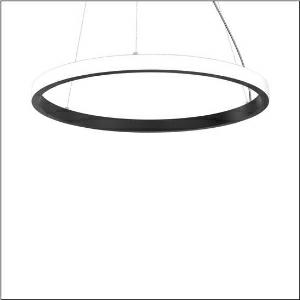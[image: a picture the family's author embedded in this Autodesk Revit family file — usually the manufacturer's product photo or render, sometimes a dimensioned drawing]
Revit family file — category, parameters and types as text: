
# Revit family: silica_r__21_ring-o_5pjbo4d1104a_942a
name_source: partatom
category: Lighting Fixtures
units: mm (PartAtom-declared; Revit-internal decimal feet)

## family parameters
Cut with Voids When Loaded = No
Host = Face
Light Source = No
Part Type = Normal
Room Calculation Point = No
Round Connector Dimension = Use Diameter
Shared = No

## types (1)
- Silica® 21 Ring-O (1 x LED, 8820 lm, 140 W, 3000K)
    Apparent Load = 140 VA
    CIE Flux Codes = 2 16 49 50 100
    Color Rendering = 80
    Color Temperature = 3000K
    Default Elevation = 1800 mm
    Description = Silica® 21 Ring-O, suspended luminaire, of PMMA, frosted, light emission: outer ring side luminous distribution, primary light characteristic: symmetric, installation type: suspended mounting, LED, rated luminous flux: 8.820lm, luminous efficacy: 63lm/W, light colour: 830, colour temperature: 3000K, control gear: DALI 2, with terminal, 5-pole, mains connection: 230V, AC/DC, 0/50..60Hz, rated input power: 140W, housing, of extruded aluminium section, jet black (RAL 9005), diameter: 1.480mm, ceiling canopy, jet black (RAL 9005), protection rating (lamp compartment): IP40, insulation class (complete): insulation class I (protective earthing), certification: CE, impact resistance: IK02, permissible operating ambient temperature: 0..+35°C, packaging unit: 1 piece
    Height = 48 mm  [stored 0.15748 ft]
    Lamp = 1 x LED
    Lamp Light Flux = 8820 lm
    Lamp Power = 140 W
    Lamp count = 1
    Length = 1480 mm
    Luminous efficacy = 63 lm/W
    Manufacturer = Siteco
    ModVariant = No
    Model = 5PJBO4D1104A
    Mounting Place = Ceiling
    Mounting Type = Pendant
    Number of Poles = 1
    OnlyDefault = Yes
    Power Factor = 1
    Product Name = Silica® 21 Ring-O
    Product group = suspended luminaire
    ProductGroupID = 905
    Protection Class = Protection class I
    Protection Degree = IP 40
    RLX_Detail_Level = 1
    RLX_Emergency_Light_Flux = 0 lm
    RLX_Emergency_Type = 0
    RLX_Emergency_Type_DB = No
    RlxData = <blob elided: 20561 chars, md5=16fe8a7a>
    Socket = socket
    Standby Power = 0 W
    System Light Flux = 8820 lm
    System Power = 140 W
    Type Comments = Product without accessories
    Type Image = l_1258389.jpg
    URL = http://relux.com
    VarID = ---
    Voltage = 0 V
    Weight = 0.00 kg
    Width = 0 mm  [stored 0 ft]

note: [stored X ft] marks values corroborated as IEEE doubles in the binary element streams (Revit-internal decimal feet)

## geometry (parser evidence)
native form markers: Blend x4, Sweep x14
no freeform markers — native parametric forms only
